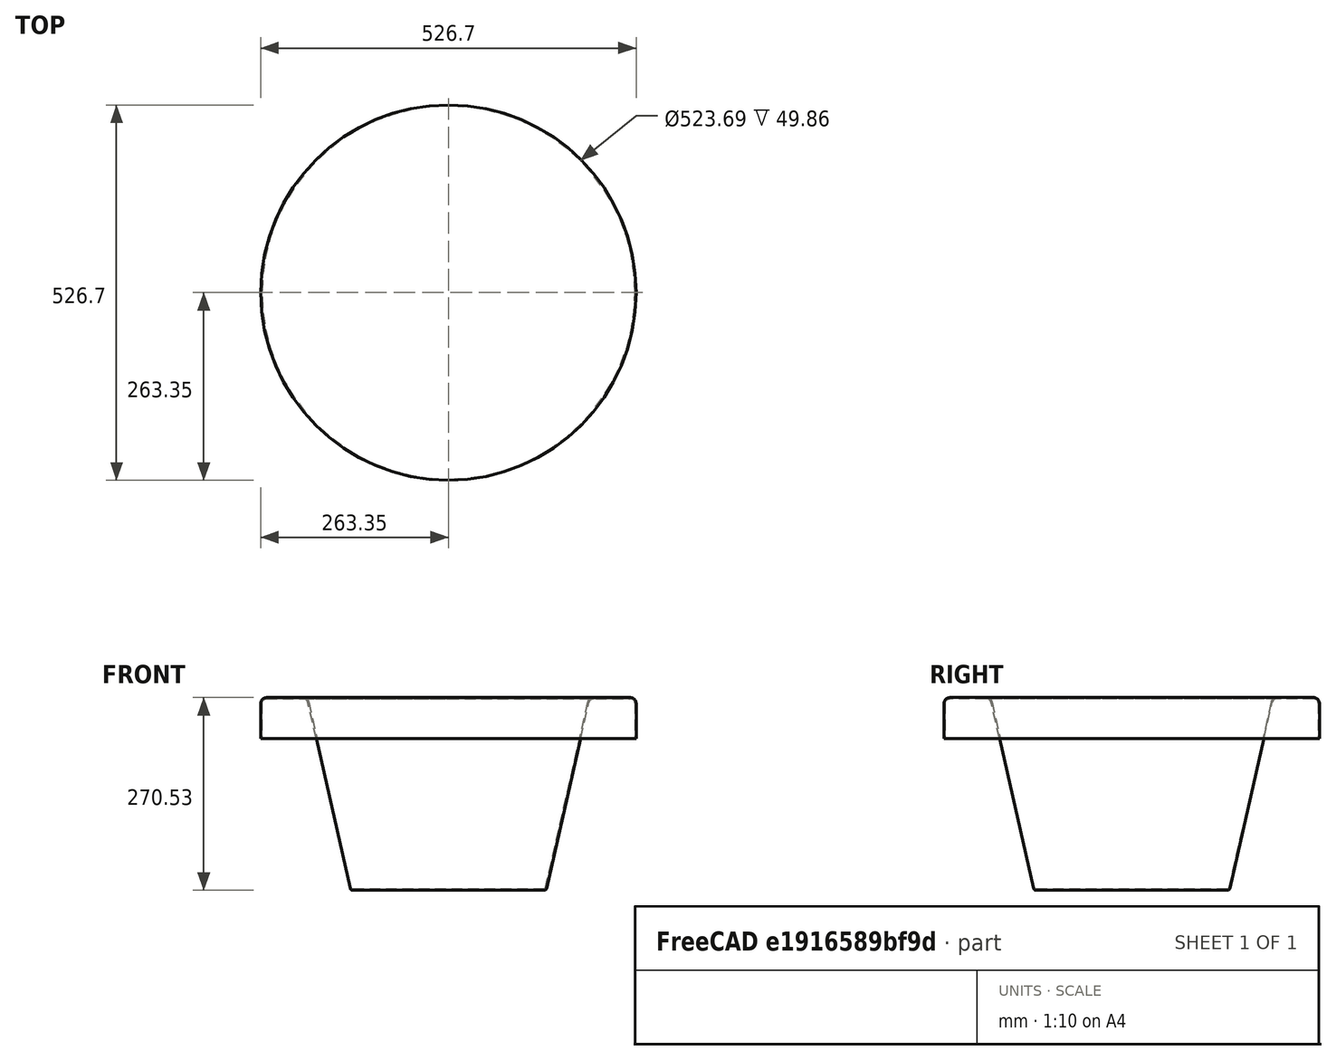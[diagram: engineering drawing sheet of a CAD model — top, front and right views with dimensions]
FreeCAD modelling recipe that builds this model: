
FCSTD DOCUMENT  (FreeCAD 0.21R32532 (Git))
Label: basin_small
License: All rights reserved
LicenseURL: http://en.wikipedia.org/wiki/All_rights_reserved
objects: Sketcher::SketchObject×1, PartDesign::Revolution×1, PartDesign::Body×1, Spreadsheet::Sheet×1
note: 4 computed .brp shape members not serialized (recipe doc carries the construction recipe); baked Part::Feature solids carry a one-line shape summary decoded from their .brp

FEATURE [Sketcher::SketchObject] Sketch
  FullyConstrained = false
  MapMode = 5
  Placement = pos=(0,0,0) rot=(0.57735,0.57735,0.57735;2.0944rad)
  Support = -> [YZ_Plane]
  sketch-geometry (24):
    g0: LineSegment StartX=0 StartY=0 StartZ=0 EndX=134.376 EndY=0 EndZ=0
    g1: LineSegment StartX=137.623 StartY=2.5903 StartZ=0 EndX=197.244 EndY=263.953 EndZ=0
    g2: LineSegment StartX=203.613 StartY=269.033 StartZ=0 EndX=255.43 EndY=269.033 EndZ=0
    g3: LineSegment StartX=261.847 StartY=262.617 StartZ=0 EndX=261.847 EndY=212.757 EndZ=0
    g4: LineSegment StartX=261.847 StartY=212.757 StartZ=0 EndX=263.347 EndY=212.757 EndZ=0
    g5: LineSegment StartX=263.347 StartY=212.757 StartZ=0 EndX=263.347 EndY=262.617 EndZ=0
    g6: LineSegment StartX=255.43 StartY=270.533 StartZ=0 EndX=203.613 EndY=270.533 EndZ=0
    g7: LineSegment StartX=195.782 StartY=264.287 StartZ=0 EndX=136.161 EndY=2.9239 EndZ=0
    g8: LineSegment StartX=134.376 StartY=1.5 StartZ=0 EndX=0 EndY=1.5 EndZ=0
    g9: LineSegment StartX=0 StartY=1.5 StartZ=0 EndX=0 EndY=0 EndZ=0
    g10: LineSegment StartX=137.032 StartY=0 StartZ=0 EndX=135.57 EndY=0.333604 EndZ=0
    g11: LineSegment StartX=261.847 StartY=269.033 StartZ=0 EndX=261.847 EndY=270.533 EndZ=0
    g12: ArcOfCircle CenterX=134.376 CenterY=3.33115 CenterZ=0 NormalX=0 NormalY=0 NormalZ=1 AngleXU=0 Radius=1.83115 StartAngle=4.71239 EndAngle=6.05891
    g13: GeomPoint X=135.836 Y=1.5 Z=0
    g14: ArcOfCircle CenterX=134.376 CenterY=3.33115 CenterZ=0 NormalX=0 NormalY=0 NormalZ=1 AngleXU=0 Radius=3.33115 StartAngle=4.71239 EndAngle=6.05891
    g15: GeomPoint X=137.032 Y=0 Z=0
    g16: ArcOfCircle CenterX=203.613 CenterY=262.5 CenterZ=0 NormalX=0 NormalY=0 NormalZ=1 AngleXU=0 Radius=6.53272 StartAngle=1.5708 EndAngle=2.91731
    g17: GeomPoint X=198.403 Y=269.033 Z=0
    g18: ArcOfCircle CenterX=203.613 CenterY=262.5 CenterZ=0 NormalX=0 NormalY=0 NormalZ=1 AngleXU=0 Radius=8.03272 StartAngle=1.5708 EndAngle=2.91731
    g19: GeomPoint X=197.207 Y=270.533 Z=0
    g20: ArcOfCircle CenterX=255.43 CenterY=262.617 CenterZ=0 NormalX=0 NormalY=0 NormalZ=1 AngleXU=0 Radius=6.41639 StartAngle=1.1e-15 EndAngle=1.5708
    g21: GeomPoint X=261.847 Y=269.033 Z=0
    g22: ArcOfCircle CenterX=255.43 CenterY=262.617 CenterZ=0 NormalX=0 NormalY=0 NormalZ=1 AngleXU=0 Radius=7.91639 StartAngle=2.5e-15 EndAngle=1.5708
    g23: GeomPoint X=263.347 Y=270.533 Z=0
  constraints (48):
    c: Coincident(g-1,g0)
    c: PointOnObject(g15,g-1)
    c: Horizontal(g2)
    c: Vertical(g3)
    c: Coincident(g3,g4)
    c: Horizontal(g4)
    c: Coincident(g4,g5)
    c: Vertical(g5)
    c: Horizontal(g6)
    c: PointOnObject(g8,g-2)
    c: Horizontal(g8)
    c: Coincident(g8,g9)
    c: Coincident(g9,g0)
    c: Parallel(g1,g7)
    c: Coincident(g10,g15)
    c: Perpendicular(g7,g10)
    c: PointOnObject(g10,g7)
    c: Coincident(g11,g21)
    c: PointOnObject(g11,g6)
    c: Vertical(g11)
    c: Equal(g4,g11)
    c: Equal(g11,g10)
    c: Equal(g10,g9)
    c: DistanceY(g9,g9) = 1.5
    c: PointOnObject(g13,g8)
    c: PointOnObject(g13,g7)
    c: Tangent(g8,g12) = 1.5708
    c: Tangent(g7,g12) = 1.5708
    c: Tangent(g0,g14) = -1.5708
    c: Tangent(g1,g14) = -1.5708
    c: Coincident(g12,g14)
    c: PointOnObject(g17,g1)
    c: PointOnObject(g17,g2)
    c: Tangent(g1,g16) = 1.5708
    c: Tangent(g2,g16) = 1.5708
    c: PointOnObject(g19,g7)
    c: PointOnObject(g19,g6)
    c: Tangent(g7,g18) = -1.5708
    c: Tangent(g6,g18) = -1.5708
    c: PointOnObject(g21,g3)
    c: Tangent(g3,g20) = 1.5708
    c: Tangent(g2,g20) = 1.5708
    c: PointOnObject(g23,g5)
    c: PointOnObject(g23,g6)
    c: Tangent(g5,g22) = -1.5708
    c: Tangent(g6,g22) = -1.5708
    c: Coincident(g20,g22)
    c: Coincident(g16,g18)
FEATURE [PartDesign::Revolution] Revolution
  Angle = 360
  Axis = (-2e-16,3e-16,1)
  Base = (0,0,0)
  Placement = pos=(0,0,0) rot=(0.57735,0.57735,0.57735;2.0944rad)
  Profile = -> Sketch
  ReferenceAxis = -> Sketch [V_Axis]
  Reversed = true
FEATURE [PartDesign::Body] Body
  Group = -> [Sketch,Revolution]
  Origin = -> Origin
  Tip = -> Revolution
FEATURE [Spreadsheet::Sheet] Spreadsheet  label="Properties"
